# Revit family: LAMP_HANCE TRACK CRI90 SUPERSPOT
name_source: partatom
category: Modelos genéricos
revit_build: Autodesk Revit 2018 (Build: 20190510_1515(x64)
units: mm (PartAtom-declared; Revit-internal decimal feet)

## family parameters
Anfitrión = Cara
Compartido = No
Corte con vacíos al cargar = No
Cota de conector redondo = Diámetro de uso
Puede alojar armadura = No
Punto de cálculo de habitación = No
Tipo de pieza = Normal

## types (8) — shared parameters
Altura tija = 63 mm  [stored 0.206693 ft]
Anchura tija = 23 mm  [stored 0.0754593 ft]
CRI = 80
Comentarios de tipo = Availability of tilting between 0º and 90º, rotation between 0º and 355º and change ring color when placed in a project.
Diameter = 65 mm  [stored 0.213255 ft]
Elevación por defecto = 1219 mm
Fabricante = LAMP
Gear = Electronic
Installation instructions = http://www.lamp.es
Insulation class = I
Lamp = COB LED
Luminaire type = Indoor - Spotlight
Manufacturer URL = http://www.lamp.es
Manufacturer country = Spain
Manufacturer name = LAMP
Model explanation = Availability of tilting between 0º and 90º, rotation between 0º and 355º and change ring color when placed in a project.
Power Supply = 220-240V 50-60Hz
Product URL = http://www.lamp.es
Profundidad tija = 8 mm  [stored 0.0262467 ft]
Protection rating = IP20
Type = HIGH POWER CREE

## per-type parameters (varying)
| type | Body height | Descripción | Efficacy | Finish | IEE | Initial color | Initial intensity | LED Lifetime | Last update | Longitud aro | Longitud cuerpo | MacAdam | Material Track | Material tija | Modelo | Photometric web file | Plum | Power | Product code | Product datasheet | Total height | Weight |
| 438LM 3000 BLACK | 135 mm  [stored 0.442913 ft] | HANCE TRACK 220 1000 WW SSP BK/BK.
HANCE TRACK 220 1000 WW SSP BK/BK. | 51 lm/W | Texturized black | A+ | 3000 K | 438 lm | 60.000 L90 | 21/02/2022 | 64 mm | 135 mm  [stored 0.442913 ft] | 3 | LAMP_Aluminio Hance Negro | LAMP_Aluminio Hance Negro | HS1TK10SS930NBB | Cuerpo Hance TRACK CRI90 (tilting) : 438LM 3000 BLACK | 9 W | 7 W | HS1TK10SS930NBB | http://www.lamp.es
-EN.pdf | 190 mm | 0.47 kg |
| 438LM 3000 WHITE | 135 mm  [stored 0.442913 ft] | HANCE TRACK 220 1000 WW SSP BK/WH. | 51 lm/W | Texturized white | A+ | 3000 K | 438 lm | 60.000 L90 | 08/08/2018 | 64 mm | 135 mm  [stored 0.442913 ft] | 3 | LAMP_Aluminio Hance Blanco | LAMP_Aluminio Hance Blanco | HS1TK10SS930NBW | Cuerpo Hance TRACK CRI90 (tilting) : 438LM 3000 WHITE | 9 W | 7 W | HS1TK10SS930NBW | http://www.lamp.es | 190 mm | 0.47 kg |
| 492LM 4000 BLACK | 135 mm  [stored 0.442913 ft] | HANCE TRACK 220 1000 NW SSP BK/BK. | 57 lm/W | Texturized black | A+ | 4000 K | 492 lm | 60.000 L90 | 08/08/2018 | 64 mm | 135 mm  [stored 0.442913 ft] | 5 | LAMP_Aluminio Hance Negro | LAMP_Aluminio Hance Negro | HS1TK10SS940NBB | Cuerpo Hance TRACK CRI90 (tilting) : 492LM 4000 BLACK | 9 W | 7 W | HS1TK10SS940NBB | http://www.lamp.es | 190 mm | 0.47 kg |
| 492LM 4000 WHITE | 135 mm  [stored 0.442913 ft] | HANCE TRACK 220 1000 NW SSP BK/WH. | 57 lm/W | Texturized white | A+ | 4000 K | 492 lm | 60.000 L90 | 08/08/2018 | 64 mm | 135 mm  [stored 0.442913 ft] | 5 | LAMP_Aluminio Hance Blanco | LAMP_Aluminio Hance Blanco | HS1TK10SS940NBW | Cuerpo Hance TRACK CRI90 (tilting) : 492LM 4000 WHITE | 9 W | 7 W | HS1TK10SS940NBW | http://www.lamp.es | 190 mm | 0.47 kg |
| 652LM 3000 BLACK | 170 mm  [stored 0.557743 ft] | HANCE TRACK 220 2000 WW SSP BK/BK. | 47 lm/W | Texturized black | A | 3000 K | 652 lm | 50.000 L80 | 08/08/2018 | 99 mm | 170 mm  [stored 0.557743 ft] | 3 | LAMP_Aluminio Hance Negro | LAMP_Aluminio Hance Negro | HS1TK20SS930NBB | Cuerpo Hance TRACK CRI90 (tilting) : 652LM 3000 BLACK | 14 W | 13 W | HS1TK20SS930NBB | http://www.lamp.es | 225 mm  [stored 0.738189 ft] | 0.65 kg |
| 652LM 3000 WHITE | 170 mm  [stored 0.557743 ft] | HANCE TRACK 220 2000 WW SSP BK/WH. | 47 lm/W | Texturized white | A | 3000 K | 652 lm | 50.000 L80 | 08/08/2018 | 99 mm | 170 mm  [stored 0.557743 ft] | 3 | LAMP_Aluminio Hance Blanco | LAMP_Aluminio Hance Blanco | HS1TK20SS930NBW | Cuerpo Hance TRACK CRI90 (tilting) : 652LM 3000 WHITE | 13 W | 13 W | HS1TK20SS930NBW | http://www.lamp.es | 225 mm  [stored 0.738189 ft] | 0.65 kg |
| 737LM 4000 BLACK | 170 mm  [stored 0.557743 ft] | HANCE TRACK 220 2000 NW SSP BK/BK. | 53 lm/W | Texturized black | A | 4000 K | 737 lm | 50.000 L80 | 08/08/2018 | 99 mm | 170 mm  [stored 0.557743 ft] | 5 | LAMP_Aluminio Hance Negro | LAMP_Aluminio Hance Negro | HS1TK20SS940NBB | Cuerpo Hance TRACK CRI90 (tilting) : 737LM 4000 BLACK | 14 W | 13 W | HS1TK20SS940NBB | http://www.lamp.es | 225 mm  [stored 0.738189 ft] | 0.65 kg |
| 737LM 4000 WHITE | 170 mm  [stored 0.557743 ft] | HANCE TRACK 220 2000 NW SSP BK/WH. | 53 lm/W | Texturized white | A | 4000 K | 737 lm | 50.000 L80 | 08/08/2018 | 99 mm | 170 mm  [stored 0.557743 ft] | 5 | LAMP_Aluminio Hance Blanco | LAMP_Aluminio Hance Blanco | HS1TK20SS940NBW | Cuerpo Hance TRACK CRI90 (tilting) : 737LM 4000 WHITE | 16 W | 13 W | HS1TK20SS940NBW | http://www.lamp.es | 225 mm  [stored 0.738189 ft] | 0.65 kg |

note: [stored X ft] marks values corroborated as IEEE doubles in the binary element streams (Revit-internal decimal feet)
